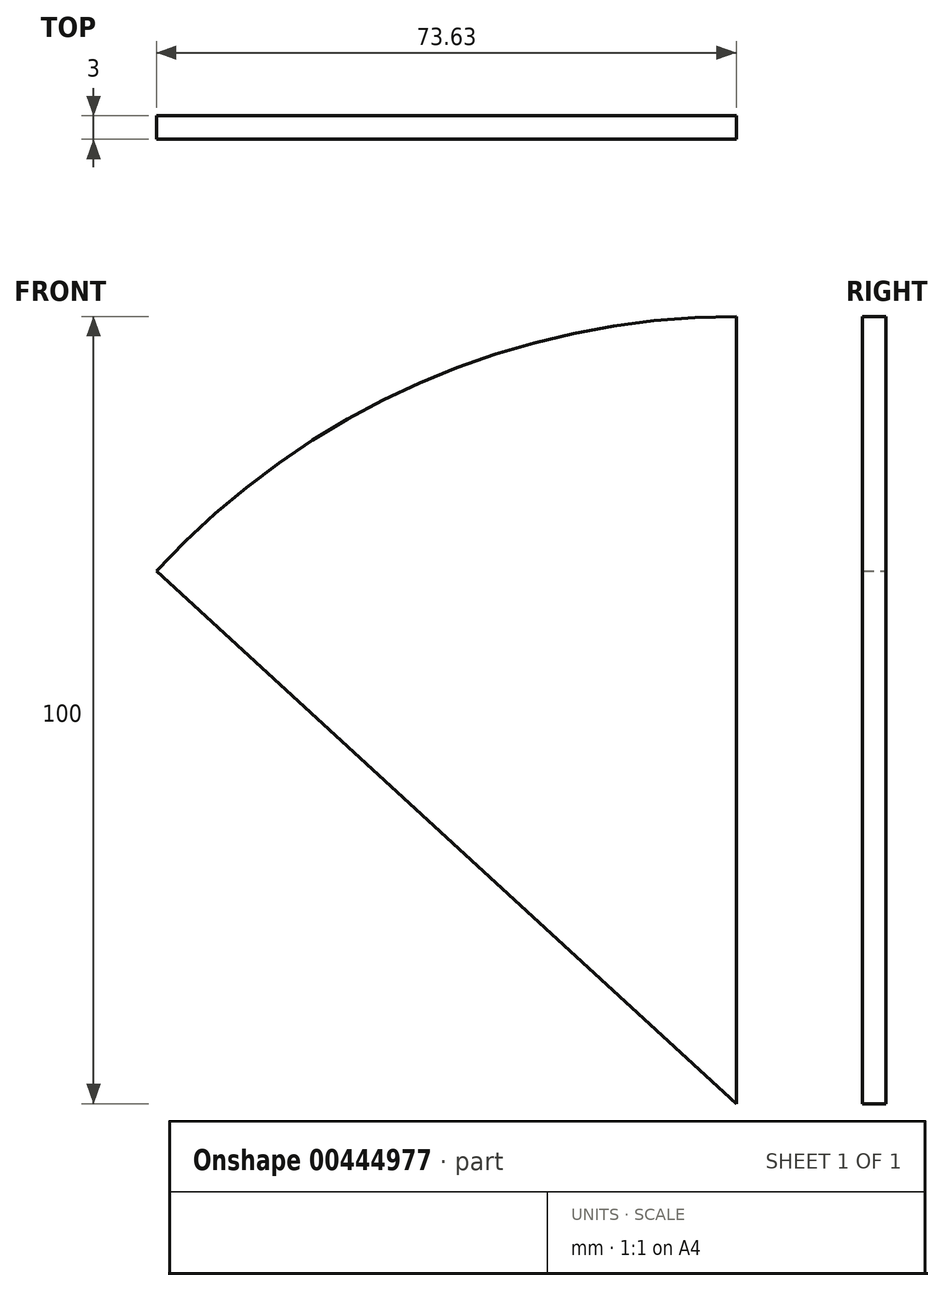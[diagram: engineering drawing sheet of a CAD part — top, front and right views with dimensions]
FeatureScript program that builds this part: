
annotation { "Feature Type Name" : "Feature", "Feature Type Description" : "" }
export const myFeature = defineFeature(function(context is Context, id is Id, definition is map)
    precondition{}
    {
        {
            var Q0;
            Q0=qCreatedBy(makeId("Front.planeOp"),FACE);
            var sketch = newSketch(context, id + "F0", { "sketchPlane" : qUnion([Q0])});
            skArc(sketch, "E0", {"start": v(-52.35, 106.66) * mm, "mid": v(-92.56, 98.21) * mm, "end": v(-125.98, 74.32) * mm});
            skLineSegment(sketch, "E1", {"start": v(-125.98, 74.32) * mm, "end": v(-52.35, 6.66) * mm});
            skLineSegment(sketch, "E2", {"start": v(-52.35, 6.66) * mm, "end": v(-52.35, 106.66) * mm});
            skSolve(sketch);
        }
        {
            var Q0;
            Q0 = qSketchRegion(id + "F0", true);
            extrude(context, id + "F1", {"entities" : qUnion([Q0]), "depth" : 3 * mm});
        }
    });
